# Revit family: Legrand Coffrets modulaires encastrés
name_source: partatom
category: Installations électriques
units: mm (PartAtom-declared; Revit-internal decimal feet)

## family parameters
Basée sur le plan de construction = Non
Conserver l'orientation des annotations = Non
Cote de connecteur circulaire = Utiliser le diamètre
Couper avec des vides une fois chargée = Non
Numéro OmniClass = 23.80.00.00
Partagée = Non
Point de calcul de pièce = Non
Titre OmniClass = Electric Power and Lighting
Toujours verticalement = Oui
Type d'élément = Normal

## types (14) — shared parameters
Conditions Générale d'Utilisation = https://export.legrand.com
Courant maxi admissible = 63 A
Fabricant = Legrand
Modèle = Coffret modulaire encastré
URL = www.legrand.com
zero-valued in all types: Elévation par défaut

## per-type parameters (varying)
- Coffret modulaire encastré 8 modules Porte plastique 001410: Assemblage Porte métal 1R=Non; Assemblage Porte métal 2R=Non; Assemblage Porte métal 3R=Non; Assemblage Porte métal 4R=Non; Assemblage Porte plastique 1R=Non; Assemblage Porte plastique 1R 8M=Oui; Assemblage Porte plastique 2R=Non; Assemblage Porte plastique 3R=Non; Assemblage Porte plastique 4R=Non; Assemblage Porte plastique transparente 1R=Non; Assemblage Porte plastique transparente 1R 8M=Non; Assemblage Porte plastique transparente 2R=Non; Assemblage Porte plastique transparente 3R=Non; Assemblage Porte plastique transparente 4R=Non; Bornier T=8 départs Icc 10kA; Coffret 001410=Oui; Coffret 001420=Non; Coffret 001511=Non; Coffret 001512=Non; Coffret 001513=Non; Coffret 001514=Non; Coffret 001521=Non; Coffret 001522=Non; Coffret 001523=Non; Coffret 001524=Non; Coffret 001531=Non; Coffret 001532=Non; Coffret 001533=Non; Coffret 001534=Non; Hauteur=228 mm  [stored 0.748031 ft]; Hauteur encastrement=213 mm  [stored 0.698819 ft]; Largeur=245 mm  [stored 0.803806 ft]; Largeur encastrement=205 mm  [stored 0.672572 ft]; Nombre de modules par rangée=8; Nombre de rangées=1; Porte métal=Non; Porte plastique=Oui; Profondeur d'encastrement=73 mm  [stored 0.239501 ft]; porte transparente=Non
- Coffret modulaire encastré 8 modules porte transparente 001420: Assemblage Porte métal 1R=Non; Assemblage Porte métal 2R=Non; Assemblage Porte métal 3R=Non; Assemblage Porte métal 4R=Non; Assemblage Porte plastique 1R=Non; Assemblage Porte plastique 1R 8M=Non; Assemblage Porte plastique 2R=Non; Assemblage Porte plastique 3R=Non; Assemblage Porte plastique 4R=Non; Assemblage Porte plastique transparente 1R=Non; Assemblage Porte plastique transparente 1R 8M=Oui; Assemblage Porte plastique transparente 2R=Non; Assemblage Porte plastique transparente 3R=Non; Assemblage Porte plastique transparente 4R=Non; Bornier T=8 départs Icc 10kA; Coffret 001410=Non; Coffret 001420=Oui; Coffret 001511=Non; Coffret 001512=Non; Coffret 001513=Non; Coffret 001514=Non; Coffret 001521=Non; Coffret 001522=Non; Coffret 001523=Non; Coffret 001524=Non; Coffret 001531=Non; Coffret 001532=Non; Coffret 001533=Non; Coffret 001534=Non; Hauteur=228 mm  [stored 0.748031 ft]; Hauteur encastrement=213 mm  [stored 0.698819 ft]; Largeur=245 mm  [stored 0.803806 ft]; Largeur encastrement=205 mm  [stored 0.672572 ft]; Nombre de modules par rangée=8; Nombre de rangées=1; Porte métal=Non; Porte plastique=Non; Profondeur d'encastrement=73 mm  [stored 0.239501 ft]; porte transparente=Oui
- Coffret modulaire encastré 12 modules Porte plastique 001511: Assemblage Porte métal 1R=Non; Assemblage Porte métal 2R=Non; Assemblage Porte métal 3R=Non; Assemblage Porte métal 4R=Non; Assemblage Porte plastique 1R=Oui; Assemblage Porte plastique 1R 8M=Non; Assemblage Porte plastique 2R=Non; Assemblage Porte plastique 3R=Non; Assemblage Porte plastique 4R=Non; Assemblage Porte plastique transparente 1R=Non; Assemblage Porte plastique transparente 1R 8M=Non; Assemblage Porte plastique transparente 2R=Non; Assemblage Porte plastique transparente 3R=Non; Assemblage Porte plastique transparente 4R=Non; Bornier T=Bornier à connexion auto 5+9 trous Icc 10kA; Coffret 001410=Non; Coffret 001420=Non; Coffret 001511=Oui; Coffret 001512=Non; Coffret 001513=Non; Coffret 001514=Non; Coffret 001521=Non; Coffret 001522=Non; Coffret 001523=Non; Coffret 001524=Non; Coffret 001531=Non; Coffret 001532=Non; Coffret 001533=Non; Coffret 001534=Non; Hauteur=335 mm  [stored 1.09908 ft]; Hauteur encastrement=305 mm  [stored 1.00066 ft]; Largeur=350 mm  [stored 1.14829 ft]; Largeur encastrement=330 mm; Nombre de modules par rangée=12+2; Nombre de rangées=1; Porte métal=Non; Porte plastique=Oui; Profondeur d'encastrement=90 mm  [stored 0.295276 ft]; porte transparente=Non
- Coffret modulaire encastré 24 modules Porte plastique 001512: Assemblage Porte métal 1R=Non; Assemblage Porte métal 2R=Non; Assemblage Porte métal 3R=Non; Assemblage Porte métal 4R=Non; Assemblage Porte plastique 1R=Non; Assemblage Porte plastique 1R 8M=Non; Assemblage Porte plastique 2R=Oui; Assemblage Porte plastique 3R=Non; Assemblage Porte plastique 4R=Non; Assemblage Porte plastique transparente 1R=Non; Assemblage Porte plastique transparente 1R 8M=Non; Assemblage Porte plastique transparente 2R=Non; Assemblage Porte plastique transparente 3R=Non; Assemblage Porte plastique transparente 4R=Non; Bornier T=Bornier à connexion auto 5+18 trous Icc 10kA; Coffret 001410=Non; Coffret 001420=Non; Coffret 001511=Non; Coffret 001512=Oui; Coffret 001513=Non; Coffret 001514=Non; Coffret 001521=Non; Coffret 001522=Non; Coffret 001523=Non; Coffret 001524=Non; Coffret 001531=Non; Coffret 001532=Non; Coffret 001533=Non; Coffret 001534=Non; Hauteur=460 mm  [stored 1.50919 ft]; Hauteur encastrement=430 mm; Largeur=350 mm  [stored 1.14829 ft]; Largeur encastrement=330 mm; Nombre de modules par rangée=12+2; Nombre de rangées=2; Porte métal=Non; Porte plastique=Oui; Profondeur d'encastrement=90 mm  [stored 0.295276 ft]; porte transparente=Non
- Coffret modulaire encastré 36 modules Porte plastique 001513: Assemblage Porte métal 1R=Non; Assemblage Porte métal 2R=Non; Assemblage Porte métal 3R=Non; Assemblage Porte métal 4R=Non; Assemblage Porte plastique 1R=Non; Assemblage Porte plastique 1R 8M=Non; Assemblage Porte plastique 2R=Non; Assemblage Porte plastique 3R=Oui; Assemblage Porte plastique 4R=Non; Assemblage Porte plastique transparente 1R=Non; Assemblage Porte plastique transparente 1R 8M=Non; Assemblage Porte plastique transparente 2R=Non; Assemblage Porte plastique transparente 3R=Non; Assemblage Porte plastique transparente 4R=Non; Bornier T=Bornier à connexion auto 5+27 trous Icc 10kA; Coffret 001410=Non; Coffret 001420=Non; Coffret 001511=Non; Coffret 001512=Non; Coffret 001513=Oui; Coffret 001514=Non; Coffret 001521=Non; Coffret 001522=Non; Coffret 001523=Non; Coffret 001524=Non; Coffret 001531=Non; Coffret 001532=Non; Coffret 001533=Non; Coffret 001534=Non; Hauteur=585 mm  [stored 1.91929 ft]; Hauteur encastrement=555 mm  [stored 1.82087 ft]; Largeur=350 mm  [stored 1.14829 ft]; Largeur encastrement=330 mm; Nombre de modules par rangée=12+2; Nombre de rangées=3; Porte métal=Non; Porte plastique=Oui; Profondeur d'encastrement=90 mm  [stored 0.295276 ft]; porte transparente=Non
- Coffret modulaire encastré 48 modules Porte plastique 001514: Assemblage Porte métal 1R=Non; Assemblage Porte métal 2R=Non; Assemblage Porte métal 3R=Non; Assemblage Porte métal 4R=Non; Assemblage Porte plastique 1R=Non; Assemblage Porte plastique 1R 8M=Non; Assemblage Porte plastique 2R=Non; Assemblage Porte plastique 3R=Non; Assemblage Porte plastique 4R=Oui; Assemblage Porte plastique transparente 1R=Non; Assemblage Porte plastique transparente 1R 8M=Non; Assemblage Porte plastique transparente 2R=Non; Assemblage Porte plastique transparente 3R=Non; Assemblage Porte plastique transparente 4R=Non; Bornier T=Bornier à connexion auto 5+36 trous Icc 10kA; Coffret 001410=Non; Coffret 001420=Non; Coffret 001511=Non; Coffret 001512=Non; Coffret 001513=Non; Coffret 001514=Oui; Coffret 001521=Non; Coffret 001522=Non; Coffret 001523=Non; Coffret 001524=Non; Coffret 001531=Non; Coffret 001532=Non; Coffret 001533=Non; Coffret 001534=Non; Hauteur=710 mm  [stored 2.3294 ft]; Hauteur encastrement=680 mm  [stored 2.23097 ft]; Largeur=350 mm  [stored 1.14829 ft]; Largeur encastrement=330 mm; Nombre de modules par rangée=12+2; Nombre de rangées=4; Porte métal=Non; Porte plastique=Oui; Profondeur d'encastrement=90 mm  [stored 0.295276 ft]; porte transparente=Non
- Coffret modulaire encastré 12 modules porte transparente 001521: Assemblage Porte métal 1R=Non; Assemblage Porte métal 2R=Non; Assemblage Porte métal 3R=Non; Assemblage Porte métal 4R=Non; Assemblage Porte plastique 1R=Non; Assemblage Porte plastique 1R 8M=Non; Assemblage Porte plastique 2R=Non; Assemblage Porte plastique 3R=Non; Assemblage Porte plastique 4R=Non; Assemblage Porte plastique transparente 1R=Oui; Assemblage Porte plastique transparente 1R 8M=Non; Assemblage Porte plastique transparente 2R=Non; Assemblage Porte plastique transparente 3R=Non; Assemblage Porte plastique transparente 4R=Non; Bornier T=Bornier à connexion auto 5+9 trous Icc 10kA; Coffret 001410=Non; Coffret 001420=Non; Coffret 001511=Non; Coffret 001512=Non; Coffret 001513=Non; Coffret 001514=Non; Coffret 001521=Oui; Coffret 001522=Non; Coffret 001523=Non; Coffret 001524=Non; Coffret 001531=Non; Coffret 001532=Non; Coffret 001533=Non; Coffret 001534=Non; Hauteur=335 mm  [stored 1.09908 ft]; Hauteur encastrement=305 mm  [stored 1.00066 ft]; Largeur=350 mm  [stored 1.14829 ft]; Largeur encastrement=330 mm; Nombre de modules par rangée=12+2; Nombre de rangées=1; Porte métal=Non; Porte plastique=Non; Profondeur d'encastrement=90 mm  [stored 0.295276 ft]; porte transparente=Oui
- Coffret modulaire encastré 24 modules porte transparente 001522: Assemblage Porte métal 1R=Non; Assemblage Porte métal 2R=Non; Assemblage Porte métal 3R=Non; Assemblage Porte métal 4R=Non; Assemblage Porte plastique 1R=Non; Assemblage Porte plastique 1R 8M=Non; Assemblage Porte plastique 2R=Non; Assemblage Porte plastique 3R=Non; Assemblage Porte plastique 4R=Non; Assemblage Porte plastique transparente 1R=Non; Assemblage Porte plastique transparente 1R 8M=Non; Assemblage Porte plastique transparente 2R=Oui; Assemblage Porte plastique transparente 3R=Non; Assemblage Porte plastique transparente 4R=Non; Bornier T=Bornier à connexion auto 5+18 trous Icc 10kA; Coffret 001410=Non; Coffret 001420=Non; Coffret 001511=Non; Coffret 001512=Non; Coffret 001513=Non; Coffret 001514=Non; Coffret 001521=Non; Coffret 001522=Oui; Coffret 001523=Non; Coffret 001524=Non; Coffret 001531=Non; Coffret 001532=Non; Coffret 001533=Non; Coffret 001534=Non; Hauteur=460 mm  [stored 1.50919 ft]; Hauteur encastrement=430 mm; Largeur=350 mm  [stored 1.14829 ft]; Largeur encastrement=330 mm; Nombre de modules par rangée=12+2; Nombre de rangées=2; Porte métal=Non; Porte plastique=Non; Profondeur d'encastrement=90 mm  [stored 0.295276 ft]; porte transparente=Oui
- Coffret modulaire encastré 36 modules porte transparente 001523: Assemblage Porte métal 1R=Non; Assemblage Porte métal 2R=Non; Assemblage Porte métal 3R=Non; Assemblage Porte métal 4R=Non; Assemblage Porte plastique 1R=Non; Assemblage Porte plastique 1R 8M=Non; Assemblage Porte plastique 2R=Non; Assemblage Porte plastique 3R=Non; Assemblage Porte plastique 4R=Non; Assemblage Porte plastique transparente 1R=Non; Assemblage Porte plastique transparente 1R 8M=Non; Assemblage Porte plastique transparente 2R=Non; Assemblage Porte plastique transparente 3R=Oui; Assemblage Porte plastique transparente 4R=Non; Bornier T=Bornier à connexion auto 5+27 trous Icc 10kA; Coffret 001410=Non; Coffret 001420=Non; Coffret 001511=Non; Coffret 001512=Non; Coffret 001513=Non; Coffret 001514=Non; Coffret 001521=Non; Coffret 001522=Non; Coffret 001523=Oui; Coffret 001524=Non; Coffret 001531=Non; Coffret 001532=Non; Coffret 001533=Non; Coffret 001534=Non; Hauteur=585 mm  [stored 1.91929 ft]; Hauteur encastrement=555 mm  [stored 1.82087 ft]; Largeur=350 mm  [stored 1.14829 ft]; Largeur encastrement=330 mm; Nombre de modules par rangée=12+2; Nombre de rangées=3; Porte métal=Non; Porte plastique=Non; Profondeur d'encastrement=90 mm  [stored 0.295276 ft]; porte transparente=Oui
- Coffret modulaire encastré 48 modules porte transparente 001524: Assemblage Porte métal 1R=Non; Assemblage Porte métal 2R=Non; Assemblage Porte métal 3R=Non; Assemblage Porte métal 4R=Non; Assemblage Porte plastique 1R=Non; Assemblage Porte plastique 1R 8M=Non; Assemblage Porte plastique 2R=Non; Assemblage Porte plastique 3R=Non; Assemblage Porte plastique 4R=Non; Assemblage Porte plastique transparente 1R=Non; Assemblage Porte plastique transparente 1R 8M=Non; Assemblage Porte plastique transparente 2R=Non; Assemblage Porte plastique transparente 3R=Non; Assemblage Porte plastique transparente 4R=Oui; Bornier T=Bornier à connexion auto 5+36 trous Icc 10kA; Coffret 001410=Non; Coffret 001420=Non; Coffret 001511=Non; Coffret 001512=Non; Coffret 001513=Non; Coffret 001514=Non; Coffret 001521=Non; Coffret 001522=Non; Coffret 001523=Non; Coffret 001524=Oui; Coffret 001531=Non; Coffret 001532=Non; Coffret 001533=Non; Coffret 001534=Non; Hauteur=710 mm  [stored 2.3294 ft]; Hauteur encastrement=680 mm  [stored 2.23097 ft]; Largeur=350 mm  [stored 1.14829 ft]; Largeur encastrement=330 mm; Nombre de modules par rangée=12+2; Nombre de rangées=4; Porte métal=Non; Porte plastique=Non; Profondeur d'encastrement=90 mm  [stored 0.295276 ft]; porte transparente=Oui
- Coffret modulaire encastré 12 modules Porte métal 001531: Assemblage Porte métal 1R=Oui; Assemblage Porte métal 2R=Non; Assemblage Porte métal 3R=Non; Assemblage Porte métal 4R=Non; Assemblage Porte plastique 1R=Non; Assemblage Porte plastique 1R 8M=Non; Assemblage Porte plastique 2R=Non; Assemblage Porte plastique 3R=Non; Assemblage Porte plastique 4R=Non; Assemblage Porte plastique transparente 1R=Non; Assemblage Porte plastique transparente 1R 8M=Non; Assemblage Porte plastique transparente 2R=Non; Assemblage Porte plastique transparente 3R=Non; Assemblage Porte plastique transparente 4R=Non; Bornier T=Bornier à connexion auto 5+9 trous Icc 10kA; Coffret 001410=Non; Coffret 001420=Non; Coffret 001511=Non; Coffret 001512=Non; Coffret 001513=Non; Coffret 001514=Non; Coffret 001521=Non; Coffret 001522=Non; Coffret 001523=Non; Coffret 001524=Non; Coffret 001531=Oui; Coffret 001532=Non; Coffret 001533=Non; Coffret 001534=Non; Hauteur=335 mm  [stored 1.09908 ft]; Hauteur encastrement=305 mm  [stored 1.00066 ft]; Largeur=350 mm  [stored 1.14829 ft]; Largeur encastrement=330 mm; Nombre de modules par rangée=12+2; Nombre de rangées=1; Porte métal=Oui; Porte plastique=Non; Profondeur d'encastrement=90 mm  [stored 0.295276 ft]; porte transparente=Non
- Coffret modulaire encastré 24 modules Porte métal 001532: Assemblage Porte métal 1R=Non; Assemblage Porte métal 2R=Oui; Assemblage Porte métal 3R=Non; Assemblage Porte métal 4R=Non; Assemblage Porte plastique 1R=Non; Assemblage Porte plastique 1R 8M=Non; Assemblage Porte plastique 2R=Non; Assemblage Porte plastique 3R=Non; Assemblage Porte plastique 4R=Non; Assemblage Porte plastique transparente 1R=Non; Assemblage Porte plastique transparente 1R 8M=Non; Assemblage Porte plastique transparente 2R=Non; Assemblage Porte plastique transparente 3R=Non; Assemblage Porte plastique transparente 4R=Non; Bornier T=Bornier à connexion auto 5+18 trous Icc 10kA; Coffret 001410=Non; Coffret 001420=Non; Coffret 001511=Non; Coffret 001512=Non; Coffret 001513=Non; Coffret 001514=Non; Coffret 001521=Non; Coffret 001522=Non; Coffret 001523=Non; Coffret 001524=Non; Coffret 001531=Non; Coffret 001532=Oui; Coffret 001533=Non; Coffret 001534=Non; Hauteur=460 mm  [stored 1.50919 ft]; Hauteur encastrement=430 mm; Largeur=350 mm  [stored 1.14829 ft]; Largeur encastrement=330 mm; Nombre de modules par rangée=12+2; Nombre de rangées=2; Porte métal=Oui; Porte plastique=Non; Profondeur d'encastrement=90 mm  [stored 0.295276 ft]; porte transparente=Non
- Coffret modulaire encastré 36 modules Porte métal 001533: Assemblage Porte métal 1R=Non; Assemblage Porte métal 2R=Non; Assemblage Porte métal 3R=Oui; Assemblage Porte métal 4R=Non; Assemblage Porte plastique 1R=Non; Assemblage Porte plastique 1R 8M=Non; Assemblage Porte plastique 2R=Non; Assemblage Porte plastique 3R=Non; Assemblage Porte plastique 4R=Non; Assemblage Porte plastique transparente 1R=Non; Assemblage Porte plastique transparente 1R 8M=Non; Assemblage Porte plastique transparente 2R=Non; Assemblage Porte plastique transparente 3R=Non; Assemblage Porte plastique transparente 4R=Non; Bornier T=Bornier à connexion auto 5+27 trous Icc 10kA; Coffret 001410=Non; Coffret 001420=Non; Coffret 001511=Non; Coffret 001512=Non; Coffret 001513=Non; Coffret 001514=Non; Coffret 001521=Non; Coffret 001522=Non; Coffret 001523=Non; Coffret 001524=Non; Coffret 001531=Non; Coffret 001532=Non; Coffret 001533=Oui; Coffret 001534=Non; Hauteur=585 mm  [stored 1.91929 ft]; Hauteur encastrement=555 mm  [stored 1.82087 ft]; Largeur=350 mm  [stored 1.14829 ft]; Largeur encastrement=330 mm; Nombre de modules par rangée=12+2; Nombre de rangées=3; Porte métal=Oui; Porte plastique=Non; Profondeur d'encastrement=90 mm  [stored 0.295276 ft]; porte transparente=Non
- Coffret modulaire encastré 48 modules Porte métal 001534: Assemblage Porte métal 1R=Non; Assemblage Porte métal 2R=Non; Assemblage Porte métal 3R=Non; Assemblage Porte métal 4R=Oui; Assemblage Porte plastique 1R=Non; Assemblage Porte plastique 1R 8M=Non; Assemblage Porte plastique 2R=Non; Assemblage Porte plastique 3R=Non; Assemblage Porte plastique 4R=Non; Assemblage Porte plastique transparente 1R=Non; Assemblage Porte plastique transparente 1R 8M=Non; Assemblage Porte plastique transparente 2R=Non; Assemblage Porte plastique transparente 3R=Non; Assemblage Porte plastique transparente 4R=Non; Bornier T=Bornier à connexion auto 5+36 trous Icc 10kA; Coffret 001410=Non; Coffret 001420=Non; Coffret 001511=Non; Coffret 001512=Non; Coffret 001513=Non; Coffret 001514=Non; Coffret 001521=Non; Coffret 001522=Non; Coffret 001523=Non; Coffret 001524=Non; Coffret 001531=Non; Coffret 001532=Non; Coffret 001533=Non; Coffret 001534=Oui; Hauteur=710 mm  [stored 2.3294 ft]; Hauteur encastrement=680 mm  [stored 2.23097 ft]; Largeur=350 mm  [stored 1.14829 ft]; Largeur encastrement=330 mm; Nombre de modules par rangée=12+2; Nombre de rangées=4; Porte métal=Oui; Porte plastique=Non; Profondeur d'encastrement=90 mm  [stored 0.295276 ft]; porte transparente=Non

note: [stored X ft] marks values corroborated as IEEE doubles in the binary element streams (Revit-internal decimal feet)
